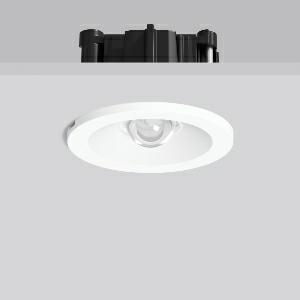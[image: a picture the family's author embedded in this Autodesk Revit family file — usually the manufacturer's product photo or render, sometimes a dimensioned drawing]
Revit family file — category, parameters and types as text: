
# Revit family: turia_l_672412_002_3d81
name_source: partatom
category: Lighting Fixtures
units: mm (PartAtom-declared; Revit-internal decimal feet)

## family parameters
Cut with Voids When Loaded = No
Host = Face
Light Source = No
Part Type = Normal
Room Calculation Point = No
Round Connector Dimension = Use Diameter
Shared = No

## types (1)
- TURIA L (1 x LED Modul 765, 270 lm, 6500)
    Apparent Load = 4 VA
    CIE Flux Codes = 16 58 99 100 100
    Color Rendering = 70
    Color Temperature = 6500
    Default Elevation = 1800 mm
    Description = Series: TURIA L
Round emergency luminaire for escape route lighting. Housing: die-cast aluminium. Bezel ring: plastic. With plastic lenses for area lighting. Self-contained system with automatic self-test. With enclosed separate ceiling mounting ring also suitable for ceiling cut-outs of Ø 68 mm. 
Colour: white
Diameter: 62 mm
Height: 3 mm
Cut-out diameter: 54-68 mm
Recess height: 76-162 mm
Luminaire: recess height: 42 mm
Weight: 420 g
Operating mode: non-maintained power mode
Duration time: 3 h
Lamp: LED
Socket: without socket
Colour temperature: 6500K
Colour rendering index (CRI): 70
System power: 4.3 W
Rated luminous flux: 270 lm
Luminous flux, emergency: 190 lm
System power, emergency: -
Control gear: Regulated power supply
Protection class: II
Type of protection: IP 20
    Height = 0 mm  [stored 0 ft]
    Lamp = 1 x LED Modul 765
    Lamp Light Flux = 270 lm
    Lamp count = 1
    Length = 62 mm  [stored 0.203412 ft]
    Lifetime = 50000 h
    Luminous efficacy = 63 lm/W
    Manufacturer = RZB
    ModVariant = No
    Model = 672412.002
    Mounting Place = Ceiling
    Mounting Type = Recessed
    Number of Poles = 1
    OnlyDefault = Yes
    Power Factor = 1
    Product Name = TURIA L
    Product group = Recessed ceiling luminaires
    ProductGroupID = 405
    Protection Class = Protection class II
    Protection Degree = IP 20
    RLX_Detail_Level = 1
    RLX_Emergency_Light_Flux = 190 lm
    RLX_Emergency_Type = 3
    RLX_Emergency_Type_DB = Yes
    RlxData = <blob elided: 35969 chars, md5=678922a4>
    Socket = socket
    Standby Power = 0 W
    System Light Flux = 270 lm
    System Power = 4 W
    Type Comments = Product without accessories
    Type Image = 672412.002.jpg
    URL = http://relux.com
    VarID = ---
    Voltage = 230 V
    Voltage Range = 220-240 V
    Weight = 0.00 kg
    Width = 0 mm  [stored 0 ft]

note: [stored X ft] marks values corroborated as IEEE doubles in the binary element streams (Revit-internal decimal feet)

## geometry (parser evidence)
native form markers: Blend x4, Sweep x11
no freeform markers — native parametric forms only
